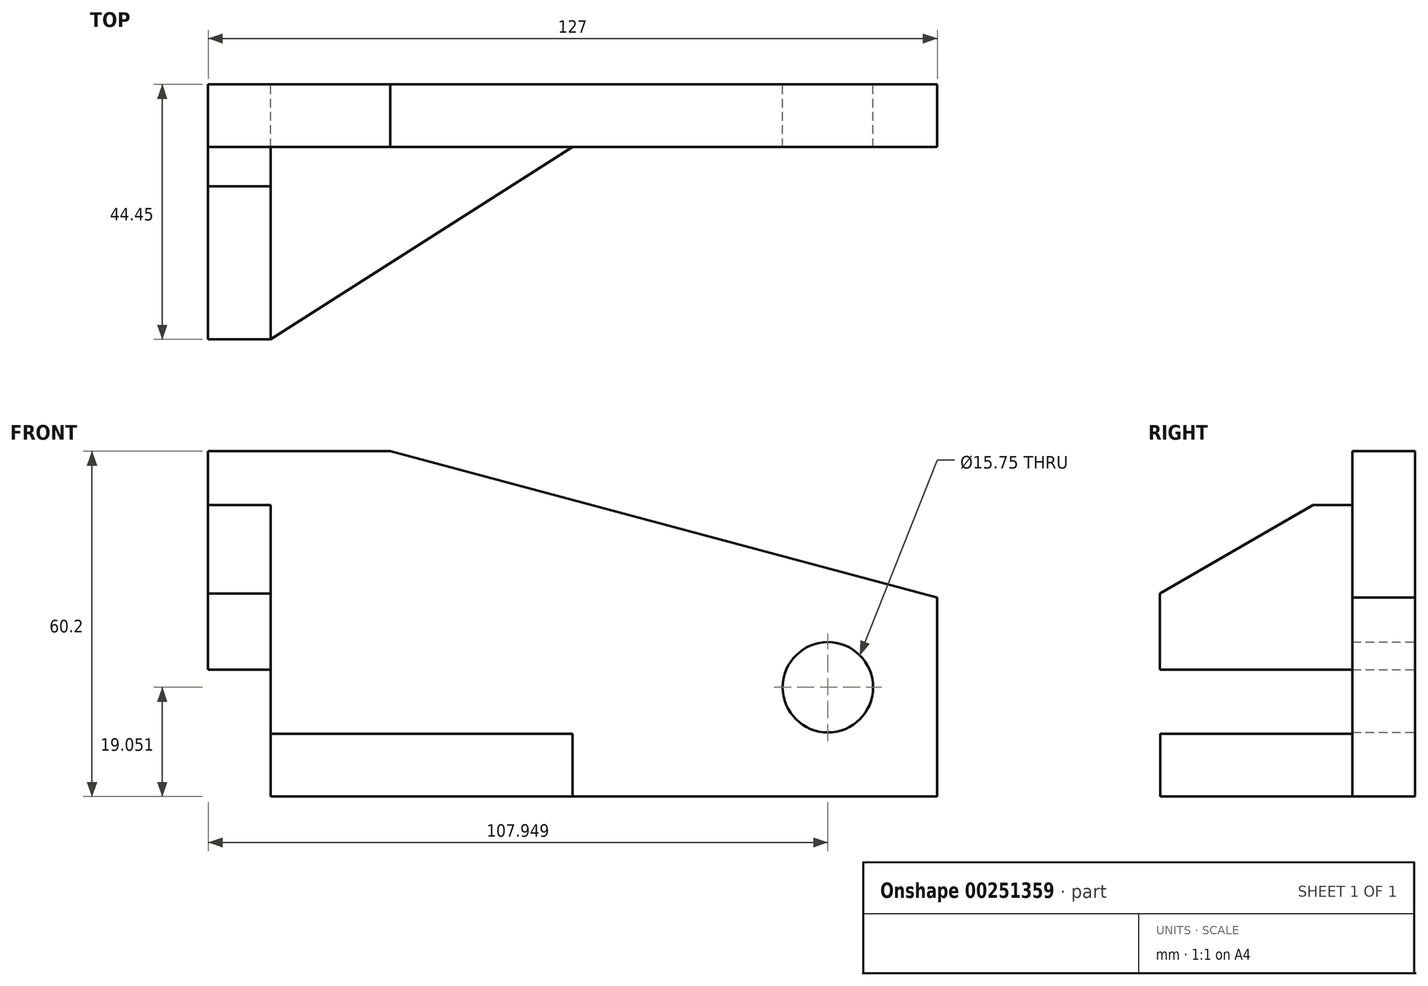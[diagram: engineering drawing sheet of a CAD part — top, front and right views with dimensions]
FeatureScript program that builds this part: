
annotation { "Feature Type Name" : "Feature", "Feature Type Description" : "" }
export const myFeature = defineFeature(function(context is Context, id is Id, definition is map)
    precondition{}
    {
        {
            var Q0;
            Q0=qCreatedBy(makeId("Front.planeOp"),FACE);
            var sketch = newSketch(context, id + "F0", { "sketchPlane" : qUnion([Q0])});
            skLineSegment(sketch, "E0.bottom", {"start": v(-45.65, 30.1) * mm, "end": v(-13.9, 30.1) * mm});
            skLineSegment(sketch, "E0.top", {"start": v(-45.65, -30.1) * mm, "end": v(81.35, -30.1) * mm});
            skLineSegment(sketch, "E0.left", {"start": v(-45.65, 30.1) * mm, "end": v(-45.65, -30.1) * mm});
            skLineSegment(sketch, "E0.right", {"start": v(81.35, 4.58) * mm, "end": v(81.35, -30.1) * mm});
            skLineSegment(sketch, "E1.top", {"start": v(-45.65, -30.1) * mm, "end": v(-34.73, -30.1) * mm});
            skLineSegment(sketch, "E2.bottom", {"start": v(-34.73, -19.18) * mm, "end": v(17.85, -19.18) * mm});
            skLineSegment(sketch, "E2.top", {"start": v(-34.73, -30.1) * mm, "end": v(17.85, -30.1) * mm});
            skLineSegment(sketch, "E2.left", {"start": v(-34.73, -19.18) * mm, "end": v(-34.73, -30.1) * mm});
            skLineSegment(sketch, "E2.right", {"start": v(17.85, -19.18) * mm, "end": v(17.85, -30.1) * mm});
            skLineSegment(sketch, "E3", {"start": v(-13.9, 30.1) * mm, "end": v(81.35, 4.58) * mm});
            skCircle(sketch, "E4", {"center": v(62.3, -11.05) * mm, "radius": 7.87 * mm});
            skLineSegment(sketch, "E5", {"start": v(-13.9, 30.1) * mm, "end": v(76.05, 30.1) * mm, "construction": true});
            skLineSegment(sketch, "E6.top", {"start": v(-45.65, 20.7) * mm, "end": v(-34.73, 20.7) * mm});
            skLineSegment(sketch, "E6.left", {"start": v(-45.65, -30.1) * mm, "end": v(-45.65, 20.7) * mm});
            skLineSegment(sketch, "E6.right", {"start": v(-34.73, -30.1) * mm, "end": v(-34.73, 20.7) * mm});
            skLineSegment(sketch, "E7.top", {"start": v(-45.65, -8) * mm, "end": v(-34.73, -8) * mm});
            skLineSegment(sketch, "E7.left", {"start": v(-45.65, -30.1) * mm, "end": v(-45.65, -8) * mm});
            skLineSegment(sketch, "E7.right", {"start": v(-34.73, -30.1) * mm, "end": v(-34.73, -8) * mm});
            skSolve(sketch);
        }
        {
            var Q0;
            Q0=makeQuery(id+"F0.imprint","IMPRINT",FACE,{"disambiguationData":[TD([[makeQuery(id+"F0.imprint","IMPRINT",EDGE,{"derivedFrom":sQuery(id+"F0.wireOp",EDGE,"E6.top")}),-1.0]])]});
            var Q1;
            {var subQ0=sQuery(id+"F0.wireOp",EDGE,"E2.bottom");Q1=makeQuery(id+"F0.imprint","IMPRINT",FACE,{"disambiguationData":[TD([[makeQuery(id+"F0.imprint","IMPRINT",EDGE,{"derivedFrom":subQ0}),-1.0]])]});}
            var Q2;
            Q2=makeQuery(id+"F0.imprint","IMPRINT",FACE,{"disambiguationData":[TD([[makeQuery(id+"F0.imprint","IMPRINT",EDGE,{"derivedFrom":sQuery(id+"F0.wireOp",EDGE,"E0.bottom")}),-1.0]])]});
            var Q3;
            {var subQ2=sQuery(id+"F0.wireOp",EDGE,"E1.top");Q3=makeQuery(id+"F0.imprint","IMPRINT",FACE,{"disambiguationData":[TD([[makeQuery(id+"F0.imprint","IMPRINT",EDGE,{"derivedFrom":subQ2}),1.0]])]});}
            extrude(context, id + "F1", {"entities" : qUnion([Q0, Q1, Q2, Q3]), "depth" : 10.92 * mm});
        }
        {
            var Q0;
            Q0=makeQuery(id+"F0.imprint","IMPRINT",FACE,{"disambiguationData":[TD([[makeQuery(id+"F0.imprint","IMPRINT",EDGE,{"derivedFrom":sQuery(id+"F0.wireOp",EDGE,"E6.top")}),-1.0]])]});
            var Q1;
            {var subQ0=sQuery(id+"F0.wireOp",EDGE,"E2.bottom");Q1=makeQuery(id+"F0.imprint","IMPRINT",FACE,{"disambiguationData":[TD([[makeQuery(id+"F0.imprint","IMPRINT",EDGE,{"derivedFrom":subQ0}),-1.0]])]});}
            var Q2;
            {var subQ2=sQuery(id+"F0.wireOp",EDGE,"E1.top");Q2=makeQuery(id+"F0.imprint","IMPRINT",FACE,{"disambiguationData":[TD([[makeQuery(id+"F0.imprint","IMPRINT",EDGE,{"derivedFrom":subQ2}),1.0]])]});}
            extrude(context, id + "F2", {"entities" : qUnion([Q0, Q1, Q2]), "operationType" : NewBodyOperationType.ADD, "depth" : 44.45 * mm});
        }
        {
            var Q0;
            Q0=makeQuery(id+"F2.opExtrude","CAP_EDGE",EDGE,{"disambiguationData":[OSD([sQuery(id+"F0.wireOp",EDGE,"E2.right")])],"isStart":false});
            chamfer(context, id + "F3", {"entities" : qUnion([Q0]), "chamferType" : ChamferType.OFFSET_ANGLE, "width" : 33.53 * mm, "oppositeDirection" : false, "angle" : 57.5 * degree, "tangentPropagation" : true});
        }
        {
            var Q0;
            Q0=makeQuery(id+"F2.opExtrude","CAP_EDGE",EDGE,{"disambiguationData":[OSD([sQuery(id+"F0.wireOp",EDGE,"E6.top")])],"isStart":false});
            chamfer(context, id + "F4", {"entities" : qUnion([Q0]), "chamferType" : ChamferType.OFFSET_ANGLE, "width" : 26.67 * mm, "oppositeDirection" : false, "angle" : 30 * degree, "tangentPropagation" : true});
        }
    });
